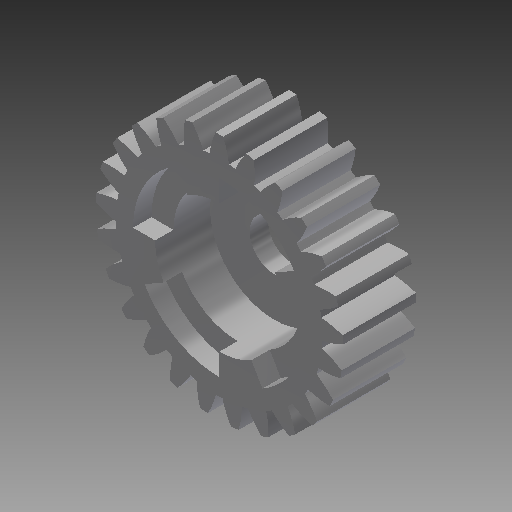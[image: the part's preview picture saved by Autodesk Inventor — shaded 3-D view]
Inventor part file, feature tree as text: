
AUTODESK INVENTOR PART (.ipt)
format: ipt  version: 2017 (Build 210142000, 142)  size: 295,936 bytes
history: native  units: mm (DEFAULTED — no unit token found)
features: sketch x5, extrude x4, plane x3, other x3, pattern_circular x1
ambient origin geometry x8: Origin, YZ Plane, XZ Plane, XY Plane, X Axis, Y Axis, Z Axis, Center Point
bodies: Solid1 (feature_tree)
feature tree (16):
  extrude  "Extrusion1"  Depth=20.0mm TaperAngle=0.0deg
  plane  "Work Plane2"
  plane  "Work Plane8"
  plane  "Work Plane9"
  other  "Spur Gear"
  extrude  "Extrusion2"  Depth=10.0mm TaperAngle=0.0deg
  extrude  "Extrusion3"  Depth=1.256637mm TaperAngle=0.0deg
  extrude  "Extrusion4"  TaperAngle=0.0deg  [1 undecoded]
  pattern_circular  "Circular Pattern1"  Count=8  [1 undecoded]
  sketch  "Sketch1"  dims[d0=67.5mm d1=20.0mm d2=0.0mm]
  sketch  "Sketch2"  dims[d3=62.5mm d4=10.0mm d5=0.0mm]
  other  "Srf1"
  sketch  "Sketch3"  dims[d16=80.0mm d17=0.0mm d34=1.256637mm]
  sketch  "Sketch4"  dims[d39=0.0mm d41=0.0mm d43=80.0mm]
  sketch  "Sketch5"  dims[d46=80.0mm d47=0.0mm d48=0.0mm d49=13.5mm d50=10.0mm d51=0.0mm d52=35.0mm d53=15.0mm d54=0.0mm d55=6.0mm d56=60.0deg d57=5.0mm d58=0.0mm d59=40.0mm d60=360.0deg]
  other  "Pitch Diameter"
note: 2 required parameter values undecoded (feature->parameter linkage not recoverable at this tier; creation-order binding heuristic only, values carry confidence <= 0.55)
